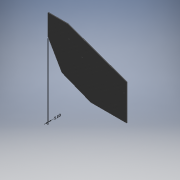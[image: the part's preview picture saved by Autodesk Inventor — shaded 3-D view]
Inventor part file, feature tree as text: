
AUTODESK INVENTOR PART (.ipt)
format: ipt  version: 2018 (Build 220112000, 112)  size: 167,424 bytes
history: native  units: mm
features: other x5, reference x4, extrude x3, sketch x3, chamfer x1
ambient origin geometry x8: Origin, YZ Plane, XZ Plane, XY Plane, X Axis, Y Axis, Z Axis, Center Point
bodies: Body1 (feature_tree)
feature tree (16):
  other  "ソリッド1"
  extrude  "押し出し1"  Depth=600.0mm
  extrude  "押し出し4"  Depth=560.0mm
  extrude  "押し出し5"  Depth=5.0mm TaperAngle=0.0deg
  chamfer  "面取り2"  Distance=5.0mm
  sketch  "スケッチ1"
  sketch  "スケッチ3"
  sketch  "スケッチ5"
  reference  "参照1"
  reference  "参照2"
  reference  "参照3"
  reference  "参照4"
  other  "<userpath>\Documents\Inventor\AeroCAD2018\設計\Rr.wing\model.iam"
  other  "model.iam"
  other  "endplate:1"
  other  "長さ寸法 1"
